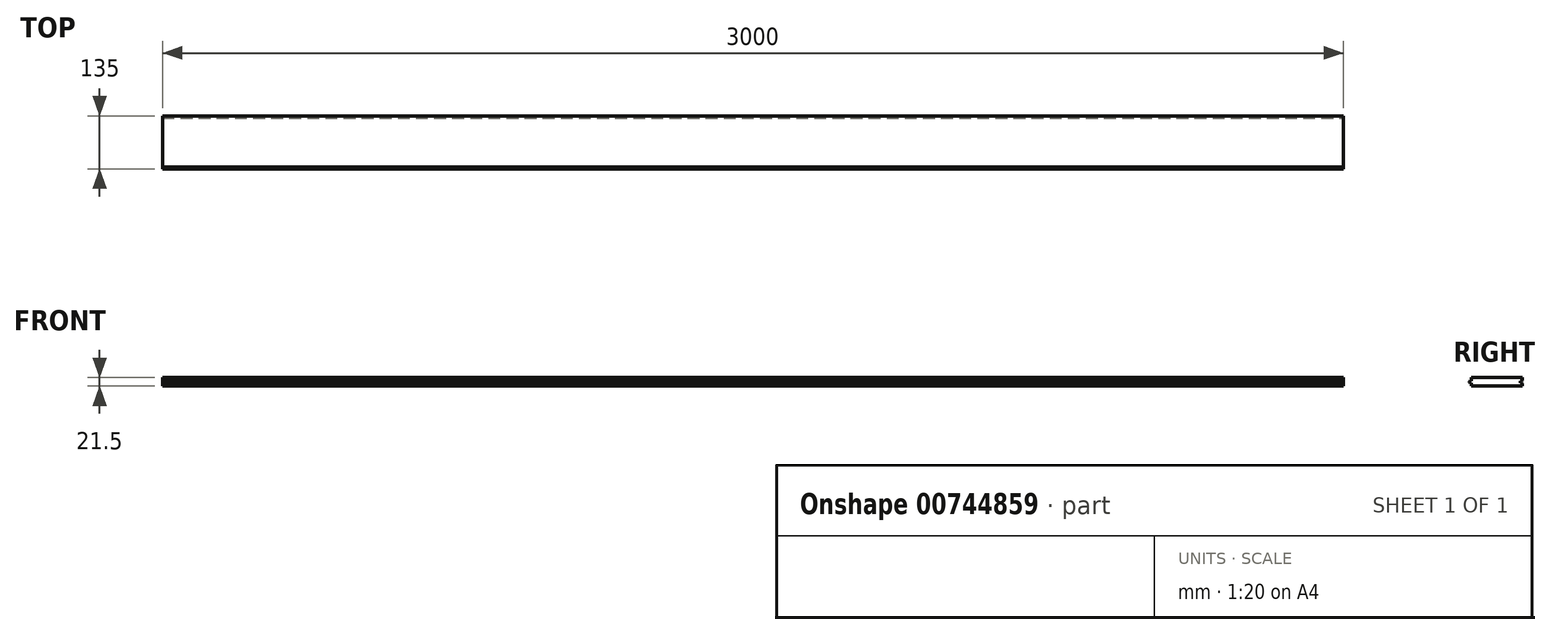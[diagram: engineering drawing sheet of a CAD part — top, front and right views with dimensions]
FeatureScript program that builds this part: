
annotation { "Feature Type Name" : "Feature", "Feature Type Description" : "" }
export const myFeature = defineFeature(function(context is Context, id is Id, definition is map)
    precondition{}
    {
        {
            var Q0;
            Q0=qCreatedBy(makeId("Right.planeOp"),FACE);
            var sketch = newSketch(context, id + "F0", { "sketchPlane" : qUnion([Q0])});
            skLineSegment(sketch, "E0", {"start": v(0, 0) * mm, "end": v(130, 0) * mm});
            skLineSegment(sketch, "E1", {"start": v(130, 0) * mm, "end": v(130, 8) * mm});
            skLineSegment(sketch, "E2", {"start": v(130, 8) * mm, "end": v(125, 8) * mm});
            skLineSegment(sketch, "E3", {"start": v(125, 8) * mm, "end": v(125, 13) * mm});
            skLineSegment(sketch, "E4", {"start": v(125, 13) * mm, "end": v(130, 13) * mm});
            skLineSegment(sketch, "E5", {"start": v(130, 13) * mm, "end": v(130, 21.5) * mm});
            skLineSegment(sketch, "E6", {"start": v(130, 21.5) * mm, "end": v(0, 21.5) * mm});
            skLineSegment(sketch, "E7", {"start": v(0, 21.5) * mm, "end": v(0, 13) * mm});
            skLineSegment(sketch, "E8", {"start": v(0, 13) * mm, "end": v(-5, 13) * mm});
            skLineSegment(sketch, "E9", {"start": v(-5, 13) * mm, "end": v(-5, 8) * mm});
            skLineSegment(sketch, "E10", {"start": v(-5, 8) * mm, "end": v(0, 8) * mm});
            skLineSegment(sketch, "E11", {"start": v(0, 8) * mm, "end": v(0, 0) * mm});
            skSolve(sketch);
        }
        {
            var Q0;
            Q0=makeQuery(id+"F0.imprint","IMPRINT",FACE,{"disambiguationData":[TD([[makeQuery(id+"F0.imprint","IMPRINT",EDGE,{"derivedFrom":sQuery(id+"F0.wireOp",EDGE,"E0")}),1.0]])]});
            extrude(context, id + "F1", {"entities" : qUnion([Q0]), "oppositeDirection" : true, "depth" : 3000 * mm, "offsetDistance" : 25 * mm});
        }
        {
            var Q0;
            Q0=makeQuery(id+"F1.opExtrude","SWEPT_EDGE",EDGE,{"disambiguationData":[OSD([sQuery(id+"F0.wireOp",EDGE,"E8"),sQuery(id+"F0.wireOp",EDGE,"E9")])]});
            var Q1;
            Q1=makeQuery(id+"F1.opExtrude","SWEPT_EDGE",EDGE,{"disambiguationData":[OSD([sQuery(id+"F0.wireOp",EDGE,"E9"),sQuery(id+"F0.wireOp",EDGE,"E10")])]});
            chamfer(context, id + "F2", {"entities" : qUnion([Q0, Q1]), "width" : 1 * mm, "tangentPropagation" : true});
        }
        {
            var Q0;
            Q0=makeQuery(id+"F1.opExtrude","SWEPT_EDGE",EDGE,{"disambiguationData":[OSD([sQuery(id+"F0.wireOp",EDGE,"E1"),sQuery(id+"F0.wireOp",EDGE,"E2")])]});
            var Q1;
            Q1=makeQuery(id+"F1.opExtrude","SWEPT_EDGE",EDGE,{"disambiguationData":[OSD([sQuery(id+"F0.wireOp",EDGE,"E4"),sQuery(id+"F0.wireOp",EDGE,"E5")])]});
            chamfer(context, id + "F3", {"entities" : qUnion([Q0, Q1]), "width" : 1 * mm, "tangentPropagation" : true});
        }
    });
